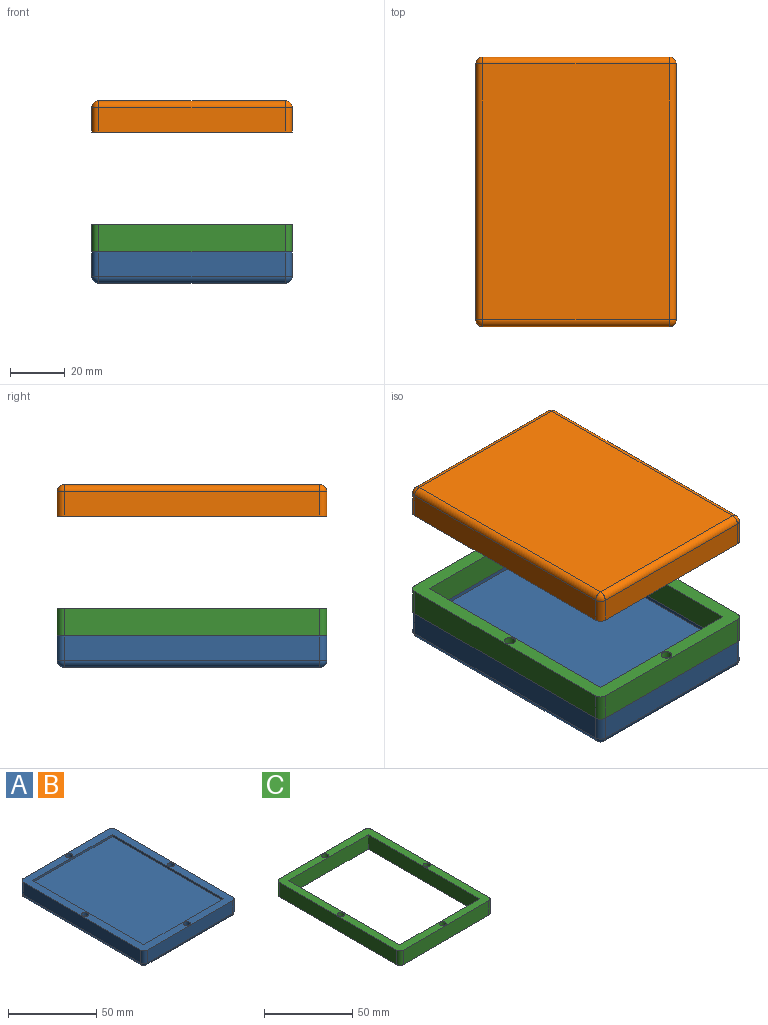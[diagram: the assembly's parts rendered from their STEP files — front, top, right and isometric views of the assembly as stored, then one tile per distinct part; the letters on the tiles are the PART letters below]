
ASSEMBLY  parts=3 mates=2
PART A: 31 faces, bbox 73.5x98.9x11.4 mm
  f0: plane 98.9x73.5mm, normal (0,0,1), area 1568.4mm2, adj f1,f2,f3,f4,f6,f7,f8,f9
  f1: plane 68.5x8.93mm, normal (0,1,0), area 611.7mm2, adj f0,f24,f28,f30
  f2: plane 93.9x8.93mm, normal (-1,0,0), area 838.5mm2, adj f0,f21,f27,f30
  f3: plane 68.5x8.93mm, normal (0,-1,0), area 611.7mm2, adj f0,f19,f21,f22
  f4: plane 93.9x8.93mm, normal (1,0,0), area 838.5mm2, adj f0,f19,f23,f24
  f5: plane 93.9x68.5mm, normal (0,0,-1), area 6432.1mm2, adj f22,f23,f27,f28
  f6: plane 63.5x1.43mm, normal (0,-1,0), area 90.8mm2, adj f0,f7,f9,f10
  f7: plane 88.9x1.43mm, normal (1,0,0), area 127.1mm2, adj f0,f6,f8,f10
  f8: plane 63.5x1.43mm, normal (0,1,0), area 90.8mm2, adj f0,f7,f9,f10
  f9: plane 88.9x1.43mm, normal (-1,0,0), area 127.1mm2, adj f0,f6,f8,f10
  f10: plane 88.9x63.5mm, normal (0,0,1), area 5645.2mm2, adj f6,f7,f8,f9
  f11: cylinder r=2mm len=4mm, axis (0,0,1), area 31.4mm2, adj f0,f12
  f12: plane 4x4mm, normal (0,0,1), area 12.6mm2, adj f11
  f13: cylinder r=2mm len=4mm, axis (0,0,1), area 31.4mm2, adj f0,f14
  f14: plane 4x4mm, normal (0,0,1), area 12.6mm2, adj f13
  f15: cylinder r=2mm len=4mm, axis (0,0,1), area 31.4mm2, adj f0,f16
  f16: plane 4x4mm, normal (0,0,1), area 12.6mm2, adj f15
  f17: cylinder r=2mm len=4mm, axis (0,0,1), area 31.4mm2, adj f0,f18
  f18: plane 4x4mm, normal (0,0,1), area 12.6mm2, adj f17
  f19: cylinder r=2.5mm len=8.93mm, axis (0,0,1), area 35.1mm2, adj f0,f3,f4,f20
  f20: sphere r=2.5mm, area 9.8mm2, adj f19,f22,f23
  f21: cylinder r=2.5mm len=8.93mm, axis (0,0,-1), area 35.1mm2, adj f0,f2,f3,f25
  f22: cylinder r=2.5mm len=68.5mm, axis (1,0,0), area 269mm2, adj f3,f5,f20,f25
  f23: cylinder r=2.5mm len=93.9mm, axis (0,1,0), area 368.7mm2, adj f4,f5,f20,f26
  f24: cylinder r=2.5mm len=8.93mm, axis (0,0,-1), area 35.1mm2, adj f0,f1,f4,f26
  f25: sphere r=2.5mm, area 9.8mm2, adj f21,f22,f27
  f26: sphere r=2.5mm, area 9.8mm2, adj f23,f24,f28
  f27: cylinder r=2.5mm len=93.9mm, axis (0,-1,0), area 368.7mm2, adj f2,f5,f25,f29
  f28: cylinder r=2.5mm len=68.5mm, axis (-1,0,0), area 269mm2, adj f1,f5,f26,f29
  f29: sphere r=2.5mm, area 9.8mm2, adj f27,f28,f30
  f30: cylinder r=2.5mm len=8.93mm, axis (0,0,1), area 35.1mm2, adj f0,f1,f2,f29
PART B: same geometry as A
PART C: 22 faces, bbox 73.5x98.9x10 mm
  f0: plane 88.9x10mm, normal (1,0,0), area 889mm2, adj f1,f7,f8,f9
  f1: plane 63.5x10mm, normal (0,-1,0), area 635mm2, adj f0,f2,f8,f9
  f2: plane 88.9x10mm, normal (-1,0,0), area 889mm2, adj f1,f7,f8,f9
  f3: plane 68.5x10mm, normal (0,1,0), area 685mm2, adj f8,f9,f18,f21
  f4: plane 93.9x10mm, normal (-1,0,0), area 939mm2, adj f8,f9,f18,f19
  f5: plane 68.5x10mm, normal (0,-1,0), area 685mm2, adj f8,f9,f19,f20
  f6: plane 93.9x10mm, normal (1,0,0), area 939mm2, adj f8,f9,f20,f21
  f7: plane 63.5x10mm, normal (0,1,0), area 635mm2, adj f0,f2,f8,f9
  f8: plane 98.9x73.5mm, normal (0,0,1), area 1568.4mm2, adj f0,f1,f2,f3,f4,f5,f6,f7
  f9: plane 98.9x73.5mm, normal (0,0,-1), area 1618.6mm2, adj f0,f1,f2,f3,f4,f5,f6,f7
  f10: cylinder r=2mm len=4mm, axis (0,0,1), area 31.4mm2, adj f8,f11
  f11: plane 4x4mm, normal (0,0,1), area 12.6mm2, adj f10
  f12: cylinder r=2mm len=4mm, axis (0,0,1), area 31.4mm2, adj f8,f13
  f13: plane 4x4mm, normal (0,0,1), area 12.6mm2, adj f12
  f14: cylinder r=2mm len=4mm, axis (0,0,1), area 31.4mm2, adj f8,f15
  f15: plane 4x4mm, normal (0,0,1), area 12.6mm2, adj f14
  f16: cylinder r=2mm len=4mm, axis (0,0,1), area 31.4mm2, adj f8,f17
  f17: plane 4x4mm, normal (0,0,1), area 12.6mm2, adj f16
  f18: cylinder r=2.5mm len=10mm, axis (0,0,1), area 39.3mm2, adj f3,f4,f8,f9
  f19: cylinder r=2.5mm len=10mm, axis (0,0,-1), area 39.3mm2, adj f4,f5,f8,f9
  f20: cylinder r=2.5mm len=10mm, axis (0,0,1), area 39.3mm2, adj f5,f6,f8,f9
  f21: cylinder r=2.5mm len=10mm, axis (0,0,-1), area 39.3mm2, adj f3,f6,f8,f9
PLACE A t=(8.85,19.66,0)mm
PLACE B rot(axis=(1,0,0),180deg) t=(8.85,121.67,66.87)mm
PLACE C t=(8.85,19.66,0)mm fixed
MATE fastened C.f9 <-> A.f0  axis (0,0,-1) through (-49.29,70.67,11.43)mm
MATE slider B.f11 <-> C.f10  axis (0,0,-1) through (-15.04,70.67,55.44)mm
